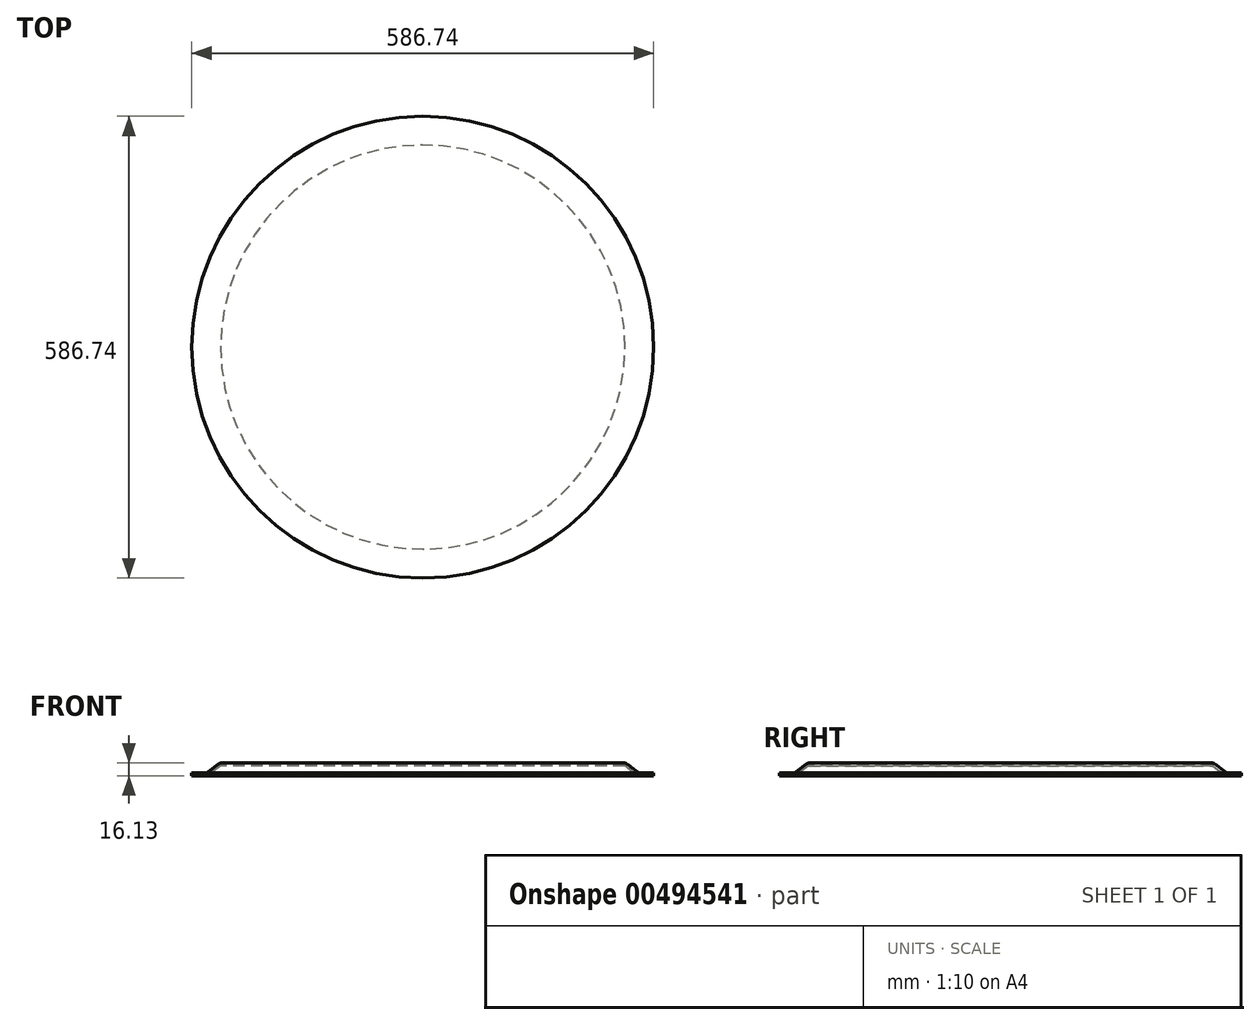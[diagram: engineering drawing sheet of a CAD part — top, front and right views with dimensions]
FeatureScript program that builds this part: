
annotation { "Feature Type Name" : "Feature", "Feature Type Description" : "" }
export const myFeature = defineFeature(function(context is Context, id is Id, definition is map)
    precondition{}
    {
        {
            var Q0;
            Q0=qCreatedBy(makeId("Front.planeOp"),FACE);
            var sketch = newSketch(context, id + "F0", { "sketchPlane" : qUnion([Q0])});
            skLineSegment(sketch, "E0", {"start": v(0, 0) * mm, "end": v(255.74, 0) * mm});
            skLineSegment(sketch, "E1", {"start": v(259.63, -1.33) * mm, "end": v(272.6, -11.37) * mm});
            skLineSegment(sketch, "E2", {"start": v(276.5, -12.7) * mm, "end": v(293.37, -12.7) * mm});
            skPoint(sketch, "E3.visualSharp", {"position": v(257.9, 0) * mm});
            skArc(sketch, "E3.filletArc", {"start": v(259.63, -1.33) * mm, "mid": v(257.8, -0.34) * mm, "end": v(255.74, 0) * mm});
            skPoint(sketch, "E4.visualSharp", {"position": v(274.32, -12.7) * mm});
            skArc(sketch, "E4.filletArc", {"start": v(272.6, -11.37) * mm, "mid": v(274.44, -12.36) * mm, "end": v(276.5, -12.7) * mm});
            skLineSegment(sketch, "E5.0", {"start": v(276.5, -16.13) * mm, "end": v(293.37, -16.13) * mm});
            skArc(sketch, "E5.1", {"start": v(270.5, -14.08) * mm, "mid": v(273.33, -15.6) * mm, "end": v(276.5, -16.13) * mm});
            skLineSegment(sketch, "E5.2", {"start": v(256.74, -3.43) * mm, "end": v(270.5, -14.08) * mm});
            skLineSegment(sketch, "E5.3", {"start": v(0, -3.43) * mm, "end": v(256.74, -3.43) * mm});
            skLineSegment(sketch, "E6", {"start": v(293.37, -12.7) * mm, "end": v(293.37, -16.13) * mm});
            skLineSegment(sketch, "E7", {"start": v(0, 0) * mm, "end": v(0, -3.43) * mm});
            skSolve(sketch);
        }
        {
            var Q0;
            Q0=makeQuery(id+"F0.imprint","IMPRINT",FACE,{"disambiguationData":[TD([[makeQuery(id+"F0.imprint","IMPRINT",EDGE,{"derivedFrom":sQuery(id+"F0.wireOp",EDGE,"E0")}),-1.0]])]});
            var Q1;
            Q1=sQuery(id+"F0.wireOp",EDGE,"E7");
            revolve(context, id + "F1", {"entities" : qUnion([Q0]), "axis" : qUnion([Q1]), "revolveType" : RevolveType.FULL});
        }
    });
